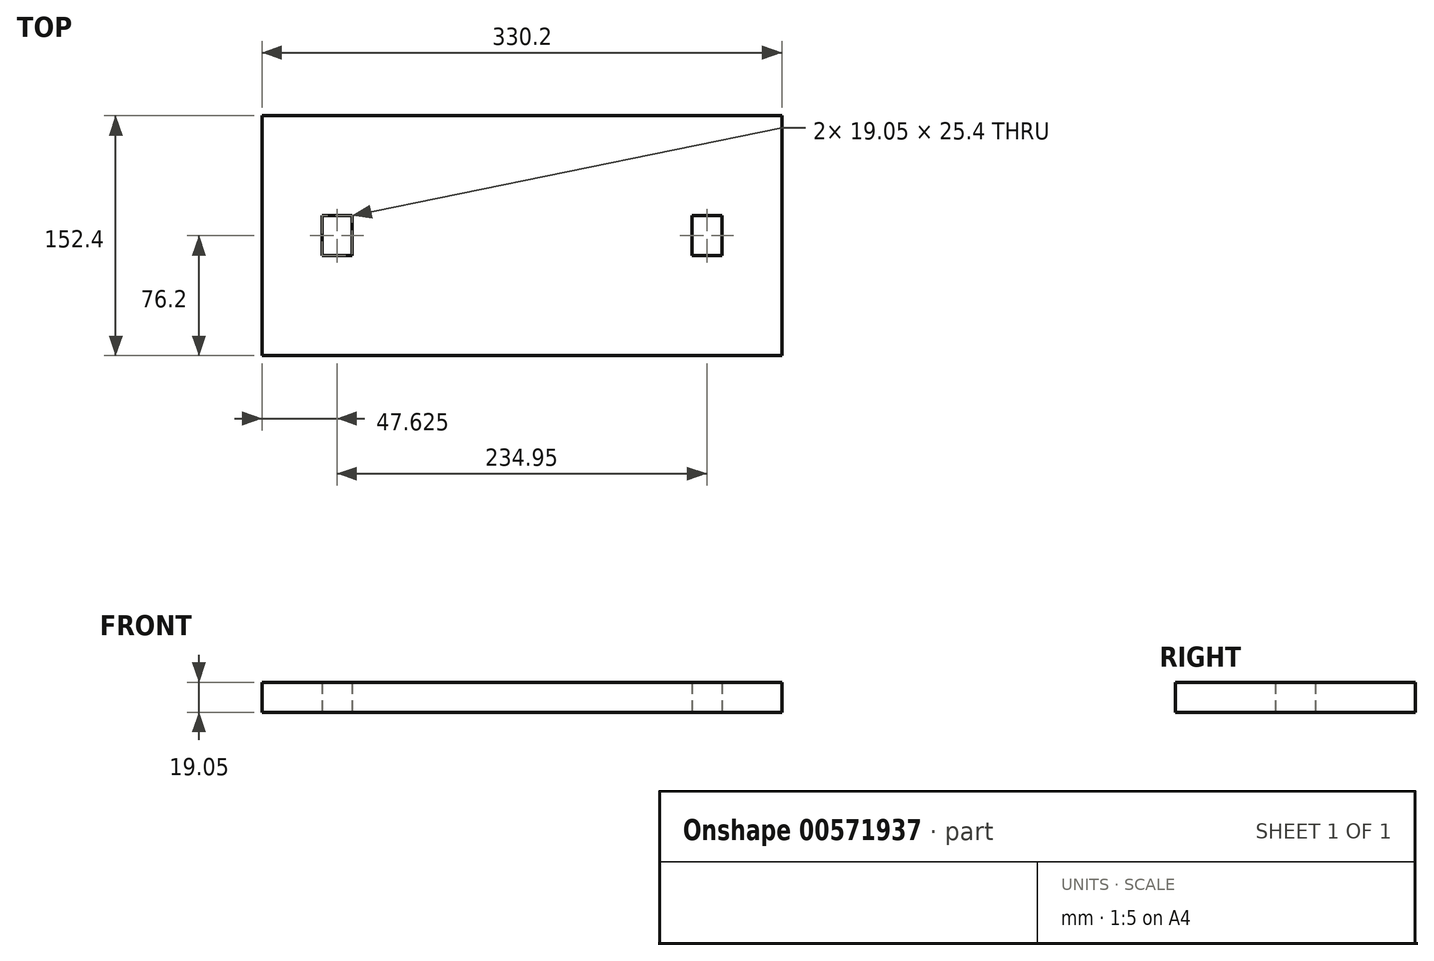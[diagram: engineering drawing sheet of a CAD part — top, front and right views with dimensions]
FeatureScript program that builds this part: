
annotation { "Feature Type Name" : "Feature", "Feature Type Description" : "" }
export const myFeature = defineFeature(function(context is Context, id is Id, definition is map)
    precondition{}
    {
        {
            var Q0;
            Q0=qCreatedBy(makeId("Top.planeOp"),FACE);
            var sketch = newSketch(context, id + "F0", { "sketchPlane" : qUnion([Q0])});
            skLineSegment(sketch, "E0.bottom", {"start": v(0, 0) * mm, "end": v(-330.2, 0) * mm});
            skLineSegment(sketch, "E0.top", {"start": v(0, -152.4) * mm, "end": v(-330.2, -152.4) * mm});
            skLineSegment(sketch, "E0.left", {"start": v(0, 0) * mm, "end": v(0, -152.4) * mm});
            skLineSegment(sketch, "E0.right", {"start": v(-330.2, 0) * mm, "end": v(-330.2, -152.4) * mm});
            skLineSegment(sketch, "E1", {"start": v(-330.2, 0) * mm, "end": v(-292.1, 0) * mm});
            skLineSegment(sketch, "E2", {"start": v(-292.1, 0) * mm, "end": v(-292.1, -152.4) * mm});
            skLineSegment(sketch, "E3", {"start": v(0, 0) * mm, "end": v(-38.1, 0) * mm});
            skLineSegment(sketch, "E4", {"start": v(-38.1, 0) * mm, "end": v(-38.1, -152.4) * mm});
            skLineSegment(sketch, "E5.bottom", {"start": v(-292.1, -88.9) * mm, "end": v(-273.05, -88.9) * mm});
            skLineSegment(sketch, "E5.top", {"start": v(-292.1, -63.5) * mm, "end": v(-273.05, -63.5) * mm});
            skLineSegment(sketch, "E5.left", {"start": v(-292.1, -88.9) * mm, "end": v(-292.1, -63.5) * mm});
            skLineSegment(sketch, "E5.right", {"start": v(-273.05, -88.9) * mm, "end": v(-273.05, -63.5) * mm});
            skLineSegment(sketch, "E6.bottom", {"start": v(-38.1, -88.9) * mm, "end": v(-57.15, -88.9) * mm});
            skLineSegment(sketch, "E6.top", {"start": v(-38.1, -63.5) * mm, "end": v(-57.15, -63.5) * mm});
            skLineSegment(sketch, "E6.left", {"start": v(-38.1, -88.9) * mm, "end": v(-38.1, -63.5) * mm});
            skLineSegment(sketch, "E6.right", {"start": v(-57.15, -88.9) * mm, "end": v(-57.15, -63.5) * mm});
            skSolve(sketch);
        }
        {
            var Q0;
            Q0 = qSketchRegion(id + "F0", true);
            extrude(context, id + "F1", {"entities" : qUnion([Q0]), "depth" : 19.05 * mm, "offsetDistance" : 25.4 * mm});
        }
    });
